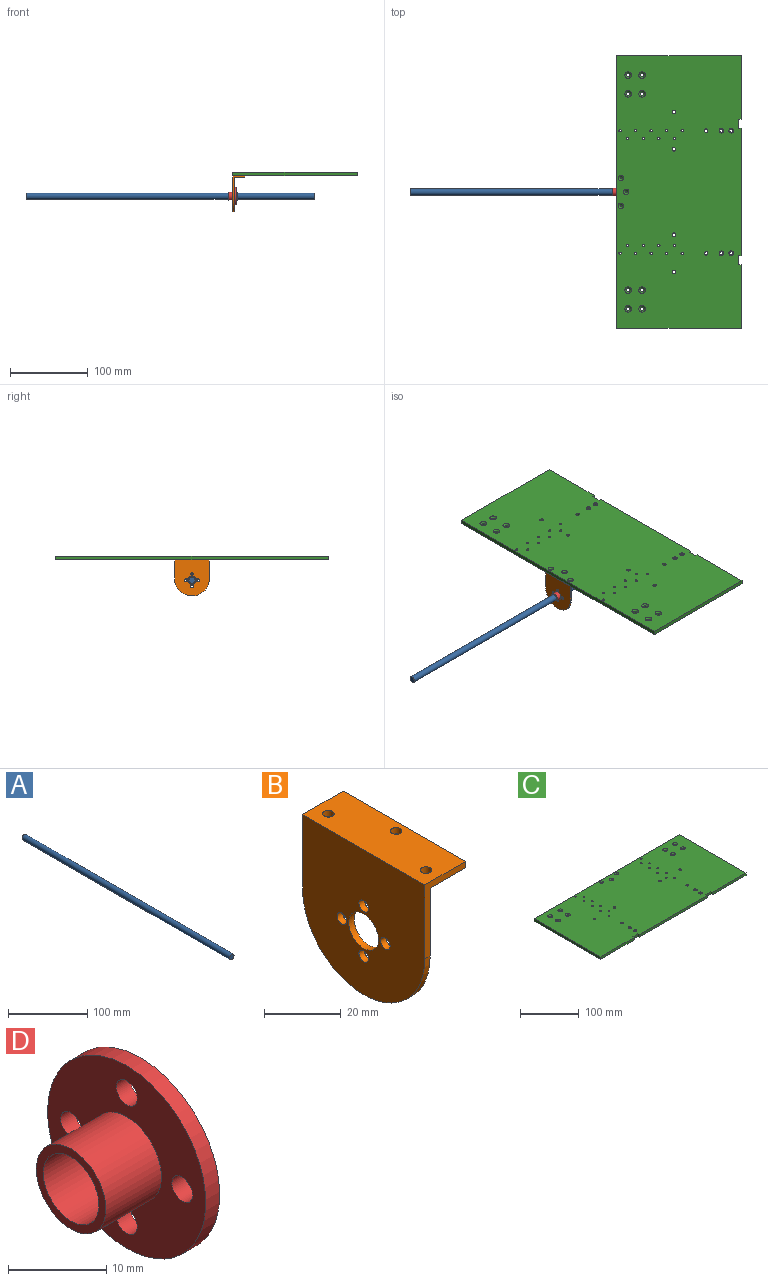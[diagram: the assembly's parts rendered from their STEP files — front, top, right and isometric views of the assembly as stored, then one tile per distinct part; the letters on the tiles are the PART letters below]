
ASSEMBLY  parts=4 mates=3
PART A: 3 faces, bbox 8x370x8 mm
  f0: cylinder r=4mm len=370mm, axis (0,1,0), area 9299.1mm2, adj f1,f2
  f1: plane 8x8mm, normal (0,-1,0), area 50.3mm2, adj f0
  f2: plane 8x8mm, normal (0,1,0), area 50.3mm2, adj f0
PART B: 16 faces, bbox 15x45x46.3 mm
  f0: plane 45x15mm, normal (0,0,1), area 653.8mm2, adj f2,f8,f11,f12,f13,f14,f15
  f1: plane 45x13mm, normal (0,0,-1), area 563.8mm2, adj f2,f8,f10,f12,f13,f14,f15
  f2: plane 23.67x15mm, normal (0,-1,0), area 73.3mm2, adj f0,f1,f3,f10,f11,f12
  f3: cylinder r=22.5mm len=45.01mm, axis (-1,0,0), area 142.9mm2, adj f2,f8,f10,f11
  f4: cylinder r=1.75mm len=3.5mm, axis (-1,0,0), area 22mm2, adj f10,f11
  f5: cylinder r=1.75mm len=3.5mm, axis (-1,0,0), area 22mm2, adj f10,f11
  f6: cylinder r=1.75mm len=3.5mm, axis (-1,0,0), area 22mm2, adj f10,f11
  f7: cylinder r=1.75mm len=3.5mm, axis (-1,0,0), area 22mm2, adj f10,f11
  f8: plane 23.15x15mm, normal (0,1,0), area 72.3mm2, adj f0,f1,f3,f10,f11,f12
  f9: cylinder r=5.5mm len=11mm, axis (-1,0,0), area 69.1mm2, adj f10,f11
  f10: plane 45.01x44.28mm, normal (1,0,0), area 1641.7mm2, adj f1,f2,f3,f4,f5,f6,f7,f8
  f11: plane 46.28x45.01mm, normal (-1,0,0), area 1731.7mm2, adj f0,f2,f3,f4,f5,f6,f7,f8
  f12: plane 45x2mm, normal (1,0,0), area 90mm2, adj f0,f1,f2,f8
  f13: cylinder r=1.5mm len=3mm, axis (0,0,1), area 18.8mm2, adj f0,f1
  f14: cylinder r=1.5mm len=3mm, axis (0,0,1), area 18.8mm2, adj f0,f1
  f15: cylinder r=1.5mm len=3mm, axis (0,0,1), area 18.8mm2, adj f0,f1
PART C: 74 faces, bbox 351x160x5 mm
  f0: plane 81.5x5mm, normal (0,-1,0), area 407.5mm2, adj f1,f4,f46,f71
  f1: plane 351x160mm, normal (0,0,-1), area 55421.6mm2, adj f0,f2,f3,f4,f5,f6,f9,f10
  f2: plane 164x5mm, normal (0,-1,0), area 820mm2, adj f1,f46,f68,f73
  f3: plane 81.5x5mm, normal (0,-1,0), area 407.5mm2, adj f1,f44,f46,f70
  f4: plane 160x5mm, normal (1,0,0), area 800mm2, adj f0,f1,f5,f46
  f5: plane 351x5mm, normal (0,1,0), area 1755mm2, adj f1,f4,f44,f46
  f6: cylinder r=2.25mm len=4.5mm, axis (0,0,-1), area 42.4mm2, adj f1,f56
  f7: cylinder r=2.25mm len=4.5mm, axis (0,0,-1), area 42.4mm2, adj f46,f55
  f8: cylinder r=2.25mm len=4.5mm, axis (0,0,-1), area 42.4mm2, adj f46,f54
  f9: cylinder r=1.5mm len=5mm, axis (0,0,-1), area 47.1mm2, adj f1,f46
  f10: cylinder r=1.5mm len=5mm, axis (0,0,-1), area 47.1mm2, adj f1,f46
  f11: cylinder r=1.5mm len=5mm, axis (0,0,-1), area 47.1mm2, adj f1,f46
  f12: cylinder r=1.5mm len=5mm, axis (0,0,-1), area 47.1mm2, adj f1,f46
  f13: cylinder r=1.5mm len=5mm, axis (0,0,-1), area 47.1mm2, adj f1,f46
  f14: cylinder r=1.5mm len=5mm, axis (0,0,-1), area 47.1mm2, adj f1,f46
  f15: cylinder r=1.5mm len=5mm, axis (0,0,-1), area 47.1mm2, adj f1,f46
  f16: cylinder r=1.5mm len=5mm, axis (0,0,-1), area 47.1mm2, adj f1,f46
  f17: cylinder r=2mm len=4mm, axis (0,0,-1), area 50.3mm2, adj f1,f65
  f18: cylinder r=1.5mm len=5mm, axis (0,0,-1), area 47.1mm2, adj f1,f46
  f19: cylinder r=1.5mm len=5mm, axis (0,0,-1), area 47.1mm2, adj f1,f46
  f20: cylinder r=1.5mm len=5mm, axis (0,0,-1), area 47.1mm2, adj f1,f46
  f21: cylinder r=1.5mm len=5mm, axis (0,0,-1), area 47.1mm2, adj f1,f46
  f22: cylinder r=1.5mm len=5mm, axis (0,0,-1), area 47.1mm2, adj f1,f46
  f23: cylinder r=1.5mm len=5mm, axis (0,0,-1), area 47.1mm2, adj f1,f46
  f24: cylinder r=1.5mm len=5mm, axis (0,0,-1), area 47.1mm2, adj f1,f46
  f25: cylinder r=2mm len=4mm, axis (0,0,-1), area 50.3mm2, adj f1,f64
  f26: cylinder r=2mm len=4mm, axis (0,0,-1), area 50.3mm2, adj f1,f66
  f27: cylinder r=2mm len=4mm, axis (0,0,-1), area 50.3mm2, adj f1,f67
  f28: cylinder r=1.5mm len=5mm, axis (0,0,-1), area 47.1mm2, adj f1,f46
  f29: cylinder r=1.5mm len=5mm, axis (0,0,-1), area 47.1mm2, adj f1,f46
  f30: cylinder r=1.5mm len=5mm, axis (0,0,-1), area 47.1mm2, adj f1,f46
  f31: cylinder r=2.25mm len=4.5mm, axis (0,0,-1), area 42.4mm2, adj f46,f53
  f32: cylinder r=2.25mm len=4.5mm, axis (0,0,-1), area 42.4mm2, adj f46,f50
  f33: cylinder r=2.25mm len=4.5mm, axis (0,0,-1), area 42.4mm2, adj f46,f51
  f34: cylinder r=2.25mm len=4.5mm, axis (0,0,-1), area 42.4mm2, adj f46,f52
  f35: cylinder r=2.25mm len=4.5mm, axis (0,0,-1), area 42.4mm2, adj f1,f59
  f36: cylinder r=2.25mm len=4.5mm, axis (0,0,-1), area 42.4mm2, adj f1,f57
  f37: cylinder r=1.5mm len=3mm, axis (0,0,-1), area 28.3mm2, adj f1,f49
  f38: cylinder r=1.5mm len=3mm, axis (0,0,-1), area 28.3mm2, adj f1,f47
  f39: cylinder r=1.5mm len=3mm, axis (0,0,-1), area 28.3mm2, adj f1,f48
  f40: cylinder r=2.25mm len=4.5mm, axis (0,0,-1), area 42.4mm2, adj f1,f60
  f41: cylinder r=2.25mm len=4.5mm, axis (0,0,-1), area 42.4mm2, adj f1,f62
  f42: cylinder r=2.25mm len=4.5mm, axis (0,0,-1), area 42.4mm2, adj f1,f61
  f43: cylinder r=2.25mm len=4.5mm, axis (0,0,-1), area 42.4mm2, adj f1,f63
  f44: plane 160x5mm, normal (-1,0,0), area 800mm2, adj f1,f3,f5,f46
  f45: cylinder r=2.25mm len=4.5mm, axis (0,0,-1), area 42.4mm2, adj f1,f58
  f46: plane 351x160mm, normal (0,0,1), area 55182.8mm2, adj f0,f2,f3,f4,f5,f7,f8,f9
  f47: cone r=1.5mm half-angle=45deg, axis (0,0,1), area 44.4mm2, adj f38,f46
  f48: cone r=1.5mm half-angle=45deg, axis (0,0,1), area 44.4mm2, adj f39,f46
  f49: cone r=1.5mm half-angle=45deg, axis (0,0,1), area 44.4mm2, adj f37,f46
  f50: cone r=4.25mm half-angle=45deg, axis (0,0,-1), area 57.8mm2, adj f1,f32
  f51: cone r=4.25mm half-angle=45deg, axis (0,0,-1), area 57.8mm2, adj f1,f33
  f52: cone r=4.25mm half-angle=45deg, axis (0,0,-1), area 57.8mm2, adj f1,f34
  f53: cone r=2.25mm half-angle=45deg, axis (0,0,-1), area 57.8mm2, adj f1,f31
  f54: cone r=2.25mm half-angle=45deg, axis (0,0,-1), area 57.8mm2, adj f1,f8
  f55: cone r=2.25mm half-angle=45deg, axis (0,0,-1), area 57.8mm2, adj f1,f7
  f56: cone r=4.25mm half-angle=45deg, axis (0,0,1), area 57.8mm2, adj f6,f46
  f57: cone r=4.25mm half-angle=45deg, axis (0,0,1), area 57.8mm2, adj f36,f46
  f58: cone r=4.25mm half-angle=45deg, axis (0,0,1), area 57.8mm2, adj f45,f46
  f59: cone r=4.25mm half-angle=45deg, axis (0,0,1), area 57.8mm2, adj f35,f46
  f60: cone r=2.25mm half-angle=45deg, axis (0,0,1), area 57.8mm2, adj f40,f46
  f61: cone r=2.25mm half-angle=45deg, axis (0,0,1), area 57.8mm2, adj f42,f46
  f62: cone r=2.25mm half-angle=45deg, axis (0,0,1), area 57.8mm2, adj f41,f46
  f63: cone r=2.25mm half-angle=45deg, axis (0,0,1), area 57.8mm2, adj f43,f46
  f64: cone r=3mm half-angle=45deg, axis (0,0,1), area 22.2mm2, adj f25,f46
  f65: cone r=3mm half-angle=45deg, axis (0,0,1), area 22.2mm2, adj f17,f46
  f66: cone r=2mm half-angle=45deg, axis (0,0,1), area 22.2mm2, adj f26,f46
  f67: cone r=2mm half-angle=45deg, axis (0,0,1), area 22.2mm2, adj f27,f46
  f68: plane 5x3mm, normal (-1,0,0), area 15mm2, adj f1,f2,f46,f69
  f69: plane 12x5mm, normal (0,-1,0), area 60mm2, adj f1,f46,f68,f70
  f70: plane 5x3mm, normal (1,0,0), area 15mm2, adj f1,f3,f46,f69
  f71: plane 5x3mm, normal (-1,0,0), area 15mm2, adj f0,f1,f46,f72
  f72: plane 12x5mm, normal (0,-1,0), area 60mm2, adj f1,f46,f71,f73
  f73: plane 5x3mm, normal (1,0,0), area 15mm2, adj f1,f2,f46,f72
PART D: 12 faces, bbox 11.5x22.7x22.7 mm
  f0: cylinder r=1.5mm len=3mm, axis (-1,0,0), area 18.8mm2, adj f5,f6
  f1: cylinder r=1.5mm len=3mm, axis (-1,0,0), area 18.8mm2, adj f5,f6
  f2: cylinder r=1.5mm len=3mm, axis (-1,0,0), area 18.8mm2, adj f5,f6
  f3: cylinder r=1.5mm len=3mm, axis (-1,0,0), area 18.8mm2, adj f5,f6
  f4: cylinder r=11.37mm len=22.75mm, axis (-1,0,0), area 142.9mm2, adj f5,f6
  f5: plane 22.75x22.75mm, normal (1,0,0), area 299.6mm2, adj f0,f1,f2,f3,f4,f9
  f6: plane 22.75x22.75mm, normal (-1,0,0), area 299.6mm2, adj f0,f1,f2,f3,f4,f7
  f7: cylinder r=5mm len=10mm, axis (1,0,0), area 251.3mm2, adj f6,f8
  f8: plane 10x10mm, normal (-1,0,0), area 28.3mm2, adj f7,f11
  f9: cylinder r=5mm len=10mm, axis (-1,0,0), area 47.1mm2, adj f5,f10
  f10: plane 10x10mm, normal (1,0,0), area 28.3mm2, adj f9,f11
  f11: cylinder r=4mm len=11.5mm, axis (1,0,0), area 289mm2, adj f8,f10
PLACE A rot(axis=(-0.69,-0.69,-0.23),154.2deg) t=(300.66,21.61,-244.82)mm
PLACE B t=(196.12,21.61,-244.82)mm
PLACE C rot(axis=(0,0,1),90deg) t=(276.12,21.61,-218.82)mm
PLACE D t=(198.12,21.61,-244.82)mm
MATE fastened B.f9 <-> D.f7  axis (1,0,0) through (198.12,21.61,-244.82)mm
MATE fastened C.f38 <-> B.f14  axis (0,0,-1) through (208.12,21.61,-218.82)mm
MATE cylindrical A.f0 <-> D.f7  axis (-1,0,0) through (-69.34,21.61,-244.82)mm
